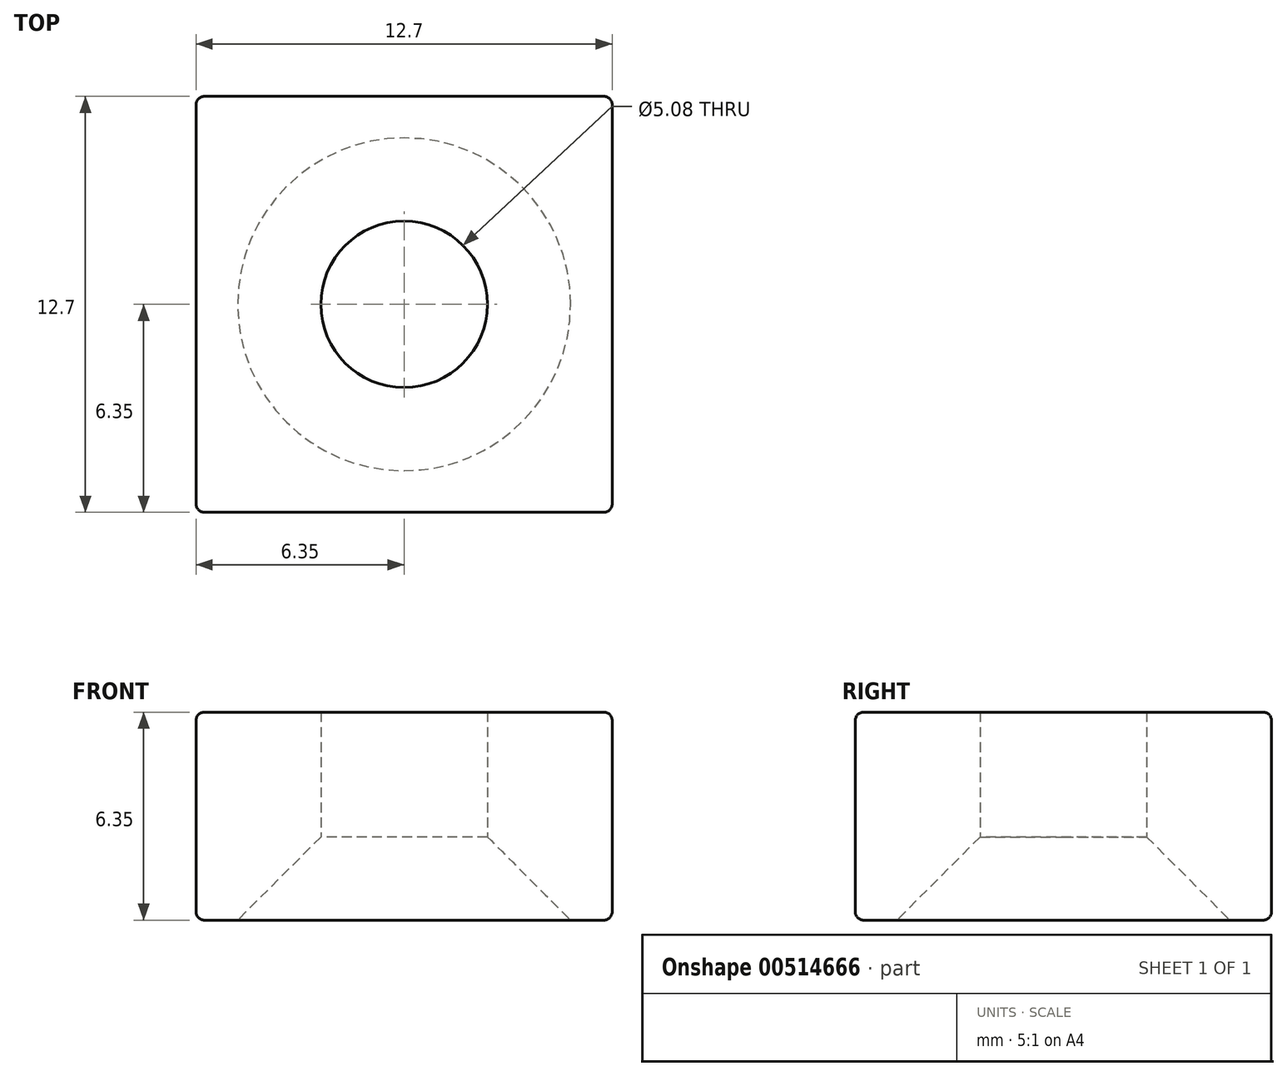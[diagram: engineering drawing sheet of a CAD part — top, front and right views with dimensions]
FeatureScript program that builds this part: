
annotation { "Feature Type Name" : "Feature", "Feature Type Description" : "" }
export const myFeature = defineFeature(function(context is Context, id is Id, definition is map)
    precondition{}
    {
        {
            var Q0;
            Q0=qCreatedBy(makeId("Top.planeOp"),FACE);
            var sketch = newSketch(context, id + "F0", { "sketchPlane" : qUnion([Q0])});
            skLineSegment(sketch, "E0.bottom", {"start": v(-6.35, 6.35) * mm, "end": v(6.35, 6.35) * mm});
            skLineSegment(sketch, "E0.top", {"start": v(-6.35, -6.35) * mm, "end": v(6.35, -6.35) * mm});
            skLineSegment(sketch, "E0.left", {"start": v(-6.35, 6.35) * mm, "end": v(-6.35, -6.35) * mm});
            skLineSegment(sketch, "E0.right", {"start": v(6.35, 6.35) * mm, "end": v(6.35, -6.35) * mm});
            skPoint(sketch, "E0.middle", {"position": v(0, 0) * mm});
            skCircle(sketch, "E1", {"center": v(0, 0) * mm, "radius": 2.54 * mm});
            skSolve(sketch);
        }
        {
            var Q0;
            Q0=makeQuery(id+"F0.imprint","IMPRINT",FACE,{"disambiguationData":[TD([[makeQuery(id+"F0.imprint","IMPRINT",EDGE,{"derivedFrom":sQuery(id+"F0.wireOp",EDGE,"E0.bottom")}),-1.0]])]});
            extrude(context, id + "F1", {"entities" : qUnion([Q0]), "depth" : 6.35 * mm, "offsetDistance" : 25.4 * mm});
        }
        {
            var Q0;
            Q0=makeQuery(id+"F1.opExtrude","CAP_EDGE",EDGE,{"disambiguationData":[OSD([sQuery(id+"F0.wireOp",EDGE,"E1")])],"isStart":true});
            chamfer(context, id + "F2", {"entities" : qUnion([Q0]), "width" : 2.54 * mm, "tangentPropagation" : true});
        }
        {
            var Q0;
            Q0=makeQuery(id+"F1.opExtrude","CAP_EDGE",EDGE,{"disambiguationData":[OSD([sQuery(id+"F0.wireOp",EDGE,"E0.top")])],"isStart":false});
            var Q1;
            Q1=makeQuery(id+"F1.opExtrude","CAP_EDGE",EDGE,{"disambiguationData":[OSD([sQuery(id+"F0.wireOp",EDGE,"E0.top")])],"isStart":true});
            var Q2;
            Q2=makeQuery(id+"F1.opExtrude","CAP_EDGE",EDGE,{"disambiguationData":[OSD([sQuery(id+"F0.wireOp",EDGE,"E0.right")])],"isStart":true});
            var Q3;
            Q3=makeQuery(id+"F1.opExtrude","CAP_EDGE",EDGE,{"disambiguationData":[OSD([sQuery(id+"F0.wireOp",EDGE,"E0.right")])],"isStart":false});
            var Q4;
            Q4=makeQuery(id+"F1.opExtrude","SWEPT_EDGE",EDGE,{"disambiguationData":[OSD([sQuery(id+"F0.wireOp",EDGE,"E0.top"),sQuery(id+"F0.wireOp",EDGE,"E0.right")])]});
            var Q5;
            Q5=makeQuery(id+"F1.opExtrude","SWEPT_EDGE",EDGE,{"disambiguationData":[OSD([sQuery(id+"F0.wireOp",EDGE,"E0.bottom"),sQuery(id+"F0.wireOp",EDGE,"E0.right")])]});
            var Q6;
            Q6=makeQuery(id+"F1.opExtrude","CAP_EDGE",EDGE,{"disambiguationData":[OSD([sQuery(id+"F0.wireOp",EDGE,"E0.bottom")])],"isStart":false});
            var Q7;
            Q7=makeQuery(id+"F1.opExtrude","SWEPT_EDGE",EDGE,{"disambiguationData":[OSD([sQuery(id+"F0.wireOp",EDGE,"E0.bottom"),sQuery(id+"F0.wireOp",EDGE,"E0.left")])]});
            var Q8;
            Q8=makeQuery(id+"F1.opExtrude","CAP_EDGE",EDGE,{"disambiguationData":[OSD([sQuery(id+"F0.wireOp",EDGE,"E0.left")])],"isStart":false});
            var Q9;
            Q9=makeQuery(id+"F1.opExtrude","SWEPT_EDGE",EDGE,{"disambiguationData":[OSD([sQuery(id+"F0.wireOp",EDGE,"E0.top"),sQuery(id+"F0.wireOp",EDGE,"E0.left")])]});
            var Q10;
            Q10=makeQuery(id+"F1.opExtrude","CAP_EDGE",EDGE,{"disambiguationData":[OSD([sQuery(id+"F0.wireOp",EDGE,"E0.left")])],"isStart":true});
            var Q11;
            Q11=makeQuery(id+"F1.opExtrude","CAP_EDGE",EDGE,{"disambiguationData":[OSD([sQuery(id+"F0.wireOp",EDGE,"E0.bottom")])],"isStart":true});
            fillet(context, id + "F3", {"entities" : qUnion([Q0, Q1, Q2, Q3, Q4, Q5, Q6, Q7, Q8, Q9, Q10, Q11]), "radius" : 0.25 * mm, "tangentPropagation" : true, "allowEdgeOverflow" : false});
        }
    });
